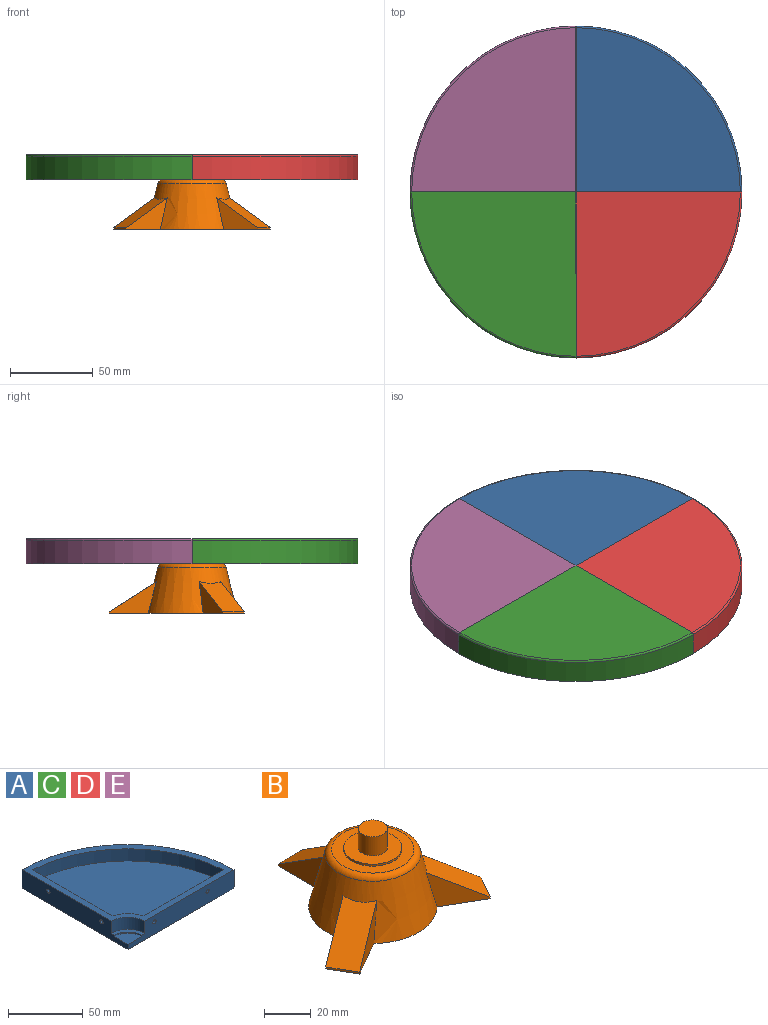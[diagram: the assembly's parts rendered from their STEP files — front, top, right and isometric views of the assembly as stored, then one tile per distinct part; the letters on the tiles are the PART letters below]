
ASSEMBLY  parts=5 mates=1
PART A: 33 faces, bbox 108.2x108.2x15 mm
  f0: plane 100x15mm, normal (0,-1,0), area 1312.6mm2, adj f4,f5,f6,f7,f8,f9,f28,f29
  f1: plane 75.5x10mm, normal (0,1,0), area 702.6mm2, adj f3,f6,f10,f13,f14,f15,f16,f17
  f2: plane 75.5x10mm, normal (1,0,0), area 740.9mm2, adj f3,f6,f10,f11,f12,f27
  f3: plane 89.87x89.87mm, normal (0,0,1), area 6022.4mm2, adj f1,f2,f10,f27
  f4: cylinder r=1.5mm len=3mm, axis (0,-1,0), area 26.4mm2, adj f0,f26
  f5: cylinder r=1.5mm len=3mm, axis (0,-1,0), area 26.4mm2, adj f0,f19
  f6: plane 100x100mm, normal (0,0,1), area 1630.5mm2, adj f0,f1,f2,f7,f8,f10,f27,f28
  f7: cylinder r=100mm len=100mm, axis (0,0,-1), area 2199.1mm2, adj f0,f6,f8,f32
  f8: plane 100x15mm, normal (-1,0,0), area 1312.6mm2, adj f0,f6,f7,f9,f11,f12,f28,f29
  f9: plane 99x99mm, normal (0,0,-1), area 7697.7mm2, adj f0,f8,f32
  f10: cylinder r=95mm len=89.87mm, axis (0,0,-1), area 1392.2mm2, adj f1,f2,f3,f6
  f11: cylinder r=1.5mm len=5mm, axis (-1,0,0), area 47.1mm2, adj f2,f8
  f12: cylinder r=1.5mm len=5mm, axis (-1,0,0), area 47.1mm2, adj f2,f8
  f13: plane 3.18x2.2mm, normal (0,0,-1), area 7mm2, adj f1,f14,f18,f19
  f14: plane 2.75x2.2mm, normal (-0.87,0,-0.5), area 7mm2, adj f1,f13,f15,f19
  f15: plane 2.75x2.2mm, normal (-0.87,0,0.5), area 7mm2, adj f1,f14,f16,f19
  f16: plane 3.18x2.2mm, normal (0,0,1), area 7mm2, adj f1,f15,f17,f19
  f17: plane 2.75x2.2mm, normal (0.87,0,0.5), area 7mm2, adj f1,f16,f18,f19
  f18: plane 2.75x2.2mm, normal (0.87,0,-0.5), area 7mm2, adj f1,f13,f17,f19
  f19: plane 6.35x5.5mm, normal (0,1,0), area 19.1mm2, adj f5,f13,f14,f15,f16,f17,f18
  f20: plane 3.18x2.2mm, normal (0,0,1), area 7mm2, adj f1,f21,f25,f26
  f21: plane 2.75x2.2mm, normal (0.87,0,0.5), area 7mm2, adj f1,f20,f22,f26
  f22: plane 2.75x2.2mm, normal (0.87,0,-0.5), area 7mm2, adj f1,f21,f23,f26
  f23: plane 3.18x2.2mm, normal (0,0,-1), area 7mm2, adj f1,f22,f24,f26
  f24: plane 2.75x2.2mm, normal (-0.87,0,-0.5), area 7mm2, adj f1,f23,f25,f26
  f25: plane 2.75x2.2mm, normal (-0.87,0,0.5), area 7mm2, adj f1,f20,f24,f26
  f26: plane 6.35x5.5mm, normal (0,1,0), area 19.1mm2, adj f4,f20,f21,f22,f23,f24,f25
  f27: cylinder r=20mm len=14.37mm, axis (0,0,-1), area 213.1mm2, adj f1,f2,f3,f6
  f28: cylinder r=16mm len=16mm, axis (0,0,1), area 251.3mm2, adj f0,f6,f8,f29
  f29: plane 16x16mm, normal (0,0,1), area 68.3mm2, adj f0,f8,f28,f30
  f30: cylinder r=13mm len=13mm, axis (0,0,1), area 20.4mm2, adj f0,f8,f29,f31
  f31: plane 13x13mm, normal (0,0,1), area 132.7mm2, adj f0,f8,f30
  f32: torus R=99mm, axis (0,0,1), area 245.8mm2, adj f0,f7,f8,f9
PART B: 32 faces, bbox 94.3x81.6x41.2 mm
  f0: plane 35.32x35.32mm, normal (0,0,1), area 488.7mm2, adj f6,f31
  f1: plane 94.1x81.5mm, normal (0,0,-1), area 1921.5mm2, adj f2,f4,f5,f10,f11,f12,f13,f14
  f2: cone r=20mm half-angle=14deg, axis (0,0,-1), area 3441.6mm2, adj f1,f13,f15,f19,f21,f25,f27,f28
  f3: plane 32.19x32.19mm, normal (0,0,-1), area 813.9mm2, adj f4
  f4: cone r=15.15mm half-angle=14deg, axis (0,0,-1), area 2755.2mm2, adj f1,f3,f5,f10,f11,f12,f16,f17
  f5: cone r=15.15mm half-angle=14deg, axis (0,0,-1), area 0.7mm2, adj f1,f4,f18
  f6: cylinder r=12.5mm len=25mm, axis (0,0,-1), area 78.5mm2, adj f0,f7
  f7: plane 25x25mm, normal (0,0,1), area 368.2mm2, adj f6,f8
  f8: cylinder r=6.25mm len=12.5mm, axis (0,0,-1), area 392.7mm2, adj f7,f9
  f9: plane 12.5x12.5mm, normal (0,0,1), area 122.7mm2, adj f8
  f10: plane 15.01x9.39mm, normal (0,-1,0), area 113.2mm2, adj f1,f4,f11,f12
  f11: plane 3.95x1.06mm, normal (-1,0,0), area 2.1mm2, adj f1,f4,f10
  f12: plane 3.95x1.06mm, normal (1,0,0), area 2.1mm2, adj f1,f4,f10
  f13: plane 28.69x19.23mm, normal (1,0,0), area 238.7mm2, adj f1,f2,f14,f28
  f14: plane 15x1mm, normal (0,1,0), area 15mm2, adj f1,f13,f15,f28
  f15: plane 28.69x19.23mm, normal (-1,0,0), area 238.7mm2, adj f1,f2,f14,f28
  f16: plane 12.99x9.39mm, normal (0.87,0.5,0), area 113.2mm2, adj f1,f4,f17,f18
  f17: plane 3.95x0.92mm, normal (0.5,-0.87,0), area 2.1mm2, adj f1,f4,f16
  f18: plane 3.95x0.92mm, normal (-0.5,0.87,0), area 2.1mm2, adj f1,f5,f16
  f19: plane 24.87x19.23mm, normal (-0.5,0.87,0), area 238.7mm2, adj f1,f2,f20,f30
  f20: plane 12.99x7.5mm, normal (-0.87,-0.5,0), area 15mm2, adj f1,f19,f21,f30
  f21: plane 24.87x19.23mm, normal (0.5,-0.87,0), area 238.7mm2, adj f1,f2,f20,f30
  f22: plane 12.99x9.39mm, normal (-0.87,0.5,0), area 113.2mm2, adj f1,f4,f23,f24
  f23: plane 3.95x0.92mm, normal (0.5,0.87,0), area 2.1mm2, adj f1,f4,f22
  f24: plane 3.95x0.92mm, normal (-0.5,-0.87,0), area 2.1mm2, adj f1,f4,f22
  f25: plane 24.87x19.23mm, normal (-0.5,-0.87,0), area 238.7mm2, adj f1,f2,f26,f29
  f26: plane 12.99x7.5mm, normal (0.87,-0.5,0), area 15mm2, adj f1,f25,f27,f29
  f27: plane 24.87x19.23mm, normal (0.5,0.87,0), area 238.7mm2, adj f1,f2,f26,f29
  f28: plane 28.54x18.08mm, normal (0,0.54,0.84), area 488.7mm2, adj f2,f13,f14,f15
  f29: plane 32.22x27.26mm, normal (0.46,-0.27,0.84), area 488.7mm2, adj f2,f25,f26,f27
  f30: plane 32.22x27.26mm, normal (-0.46,-0.27,0.84), area 488.7mm2, adj f2,f19,f20,f21
  f31: torus R=17.66mm, axis (0,0,1), area 484.1mm2, adj f0,f2
PART C: same geometry as A
PART D: same geometry as A
PART E: same geometry as A
PLACE A rot(axis=(-0.71,-0.71,0),180deg) t=(-29.89,-26.32,55.6)mm
PLACE B t=(-29.89,-26.32,10.6)mm
PLACE C rot(axis=(0.71,-0.71,0),180deg) t=(-29.89,-26.32,55.6)mm
PLACE D rot(axis=(1,0,0),180deg) t=(-29.89,-26.32,55.6)mm
PLACE E rot(axis=(0,-1,0),180deg) t=(-29.89,-26.32,55.6)mm
MATE revolute A.f30 <-> B.f8  axis (0,0,-1) through (-29.89,-26.32,51.6)mm
